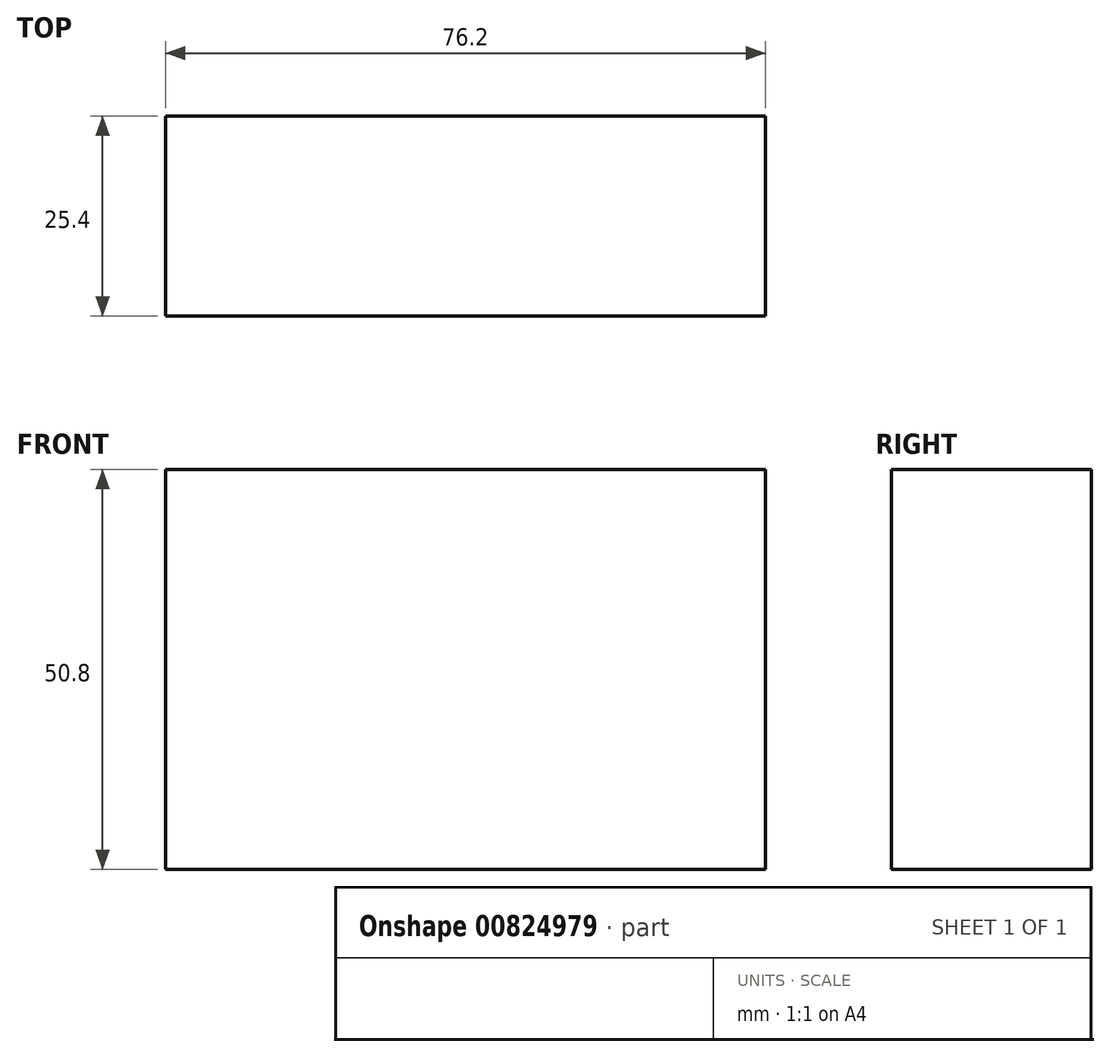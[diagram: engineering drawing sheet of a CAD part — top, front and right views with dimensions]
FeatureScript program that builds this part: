
annotation { "Feature Type Name" : "Feature", "Feature Type Description" : "" }
export const myFeature = defineFeature(function(context is Context, id is Id, definition is map)
    precondition{}
    {
        {
            var Q0;
            Q0=qCreatedBy(makeId("Front.planeOp"),FACE);
            var sketch = newSketch(context, id + "F0", { "sketchPlane" : qUnion([Q0])});
            skLineSegment(sketch, "E0", {"start": v(0, 0) * mm, "end": v(25.4, 0) * mm});
            skLineSegment(sketch, "E1", {"start": v(25.4, 0) * mm, "end": v(76.2, 0) * mm});
            skLineSegment(sketch, "E2", {"start": v(76.2, 0) * mm, "end": v(76.2, 50.8) * mm});
            skLineSegment(sketch, "E3", {"start": v(76.2, 50.8) * mm, "end": v(25.4, 50.8) * mm});
            skLineSegment(sketch, "E4", {"start": v(25.4, 50.8) * mm, "end": v(0, 50.8) * mm});
            skLineSegment(sketch, "E5", {"start": v(0, 50.8) * mm, "end": v(0, 25.4) * mm});
            skLineSegment(sketch, "E6", {"start": v(0, 25.4) * mm, "end": v(25.4, 25.4) * mm});
            skLineSegment(sketch, "E7", {"start": v(25.4, 25.4) * mm, "end": v(76.2, 25.4) * mm});
            skLineSegment(sketch, "E8", {"start": v(0, 25.4) * mm, "end": v(0, 0) * mm});
            skSolve(sketch);
        }
        {
            var Q0;
            Q0 = qSketchRegion(id + "F0", true);
            extrude(context, id + "F1", {"entities" : qUnion([Q0]), "depth" : 25.4 * mm, "offsetDistance" : 25.4 * mm});
        }
    });
